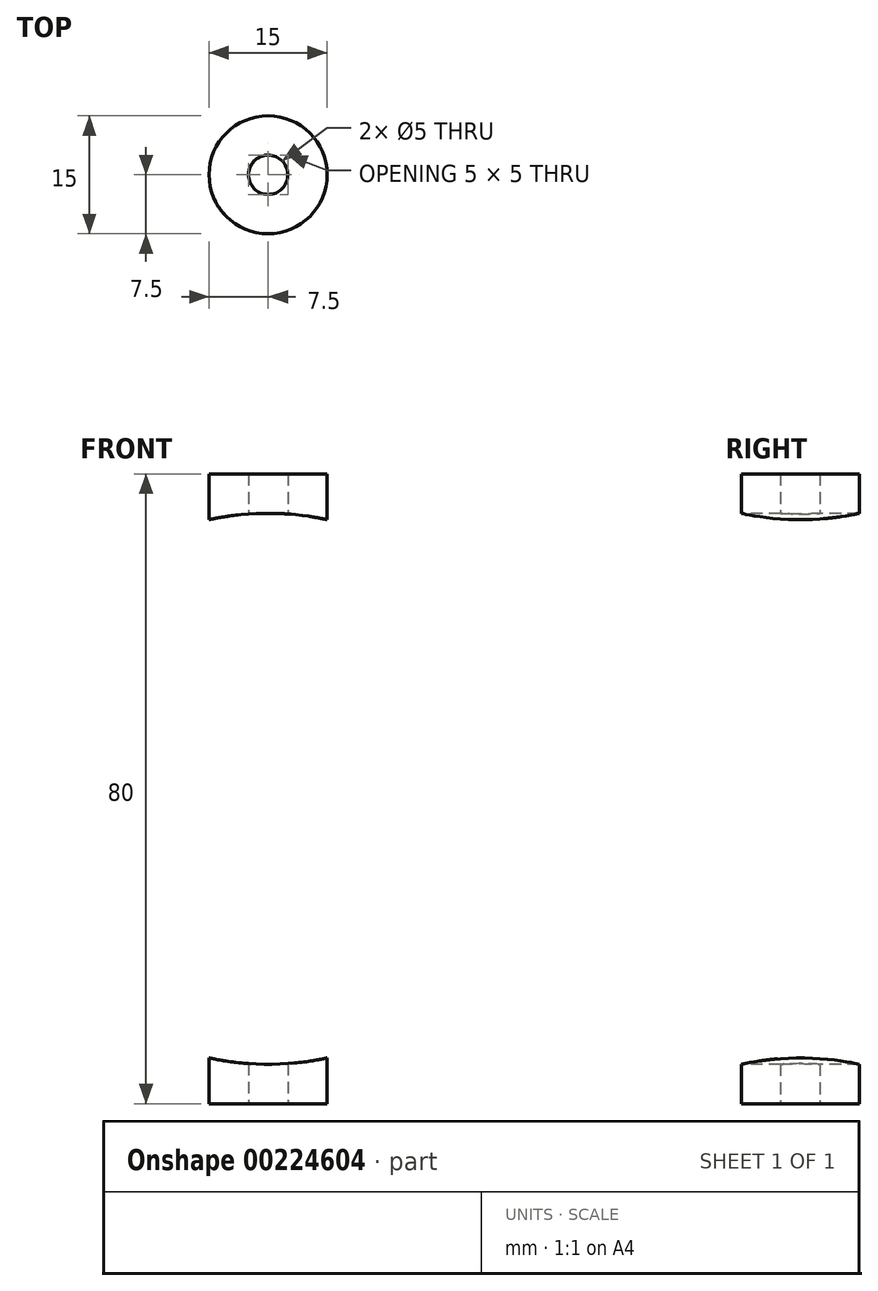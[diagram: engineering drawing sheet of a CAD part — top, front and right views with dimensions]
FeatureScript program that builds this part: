
annotation { "Feature Type Name" : "Feature", "Feature Type Description" : "" }
export const myFeature = defineFeature(function(context is Context, id is Id, definition is map)
    precondition{}
    {
        {
            var Q0;
            Q0=qCreatedBy(makeId("Front.planeOp"),FACE);
            var sketch = newSketch(context, id + "F0", { "sketchPlane" : qUnion([Q0])});
            skCircle(sketch, "E0", {"center": v(0, 40) * mm, "radius": 40 * mm});
            skCircle(sketch, "E1", {"center": v(0, 40) * mm, "radius": 35 * mm});
            skSolve(sketch);
        }
        {
            var Q0;
            Q0=qCreatedBy(makeId("Top.planeOp"),FACE);
            var sketch = newSketch(context, id + "F1", { "sketchPlane" : qUnion([Q0])});
            skCircle(sketch, "E2", {"center": v(0, 0) * mm, "radius": 2.5 * mm});
            skCircle(sketch, "E3", {"center": v(0, 0) * mm, "radius": 7.5 * mm});
            skSolve(sketch);
        }
        {
            var Q0;
            Q0=makeQuery(id+"F0.imprint","IMPRINT",FACE,{"disambiguationData":[TD([[makeQuery(id+"F0.imprint","IMPRINT",EDGE,{"derivedFrom":sQuery(id+"F0.wireOp",EDGE,"E0")}),1.0]])]});
            extrude(context, id + "F2", {"entities" : qUnion([Q0]), "endBound" : BoundingType.SYMMETRIC, "depth" : 5 * mm});
        }
        {
            var Q0;
            Q0=makeQuery(id+"F2.opExtrude","CAP_EDGE",EDGE,{"disambiguationData":[OSD([sQuery(id+"F0.wireOp",EDGE,"E0")])],"isStart":false});
            var Q1;
            Q1=makeQuery(id+"F2.opExtrude","CAP_EDGE",EDGE,{"disambiguationData":[OSD([sQuery(id+"F0.wireOp",EDGE,"E0")])],"isStart":true});
            var Q2;
            Q2=makeQuery(id+"F2.opExtrude","CAP_EDGE",EDGE,{"disambiguationData":[OSD([sQuery(id+"F0.wireOp",EDGE,"E1")])],"isStart":false});
            var Q3;
            Q3=makeQuery(id+"F2.opExtrude","CAP_EDGE",EDGE,{"disambiguationData":[OSD([sQuery(id+"F0.wireOp",EDGE,"E1")])],"isStart":true});
            fillet(context, id + "F3", {"entities" : qUnion([Q0, Q1, Q2, Q3]), "radius" : 2.5 * mm, "tangentPropagation" : true, "allowEdgeOverflow" : false});
        }
        {
            var Q0;
            Q0=makeQuery(id+"F1.imprint","IMPRINT",FACE,{"disambiguationData":[TD([[makeQuery(id+"F1.imprint","IMPRINT",EDGE,{"derivedFrom":sQuery(id+"F1.wireOp",EDGE,"E2")}),-1.0]])]});
            extrude(context, id + "F4", {"entities" : qUnion([Q0]), "operationType" : NewBodyOperationType.REMOVE, "depth" : 80 * mm});
        }
        {
            var Q0;
            Q0=makeQuery(id+"F4.boolean.opBoolean","SPLIT",BODY,{"disambiguationData":[OD(3.0)],"derivedFrom":makeQuery(id+"F2.opExtrude","SWEPT_BODY",BODY,{"disambiguationData":[OSD([sQuery(id+"F0.wireOp",EDGE,"E0"),sQuery(id+"F0.wireOp",EDGE,"E1")])]})});
            var Q1;
            Q1=makeQuery(id+"F4.boolean.opBoolean","SPLIT",BODY,{"disambiguationData":[OD(2.0)],"derivedFrom":makeQuery(id+"F2.opExtrude","SWEPT_BODY",BODY,{"disambiguationData":[OSD([sQuery(id+"F0.wireOp",EDGE,"E0"),sQuery(id+"F0.wireOp",EDGE,"E1")])]})});
            deleteBodies(context, id + "F5", {"entities" : qUnion([Q0, Q1])});
        }
        {
            var Q0;
            Q0=makeQuery(id+"F1.imprint","IMPRINT",FACE,{"disambiguationData":[TD([[makeQuery(id+"F1.imprint","IMPRINT",EDGE,{"derivedFrom":sQuery(id+"F1.wireOp",EDGE,"E2")}),-1.0]])]});
            extrude(context, id + "F6", {"entities" : qUnion([Q0]), "depth" : 80 * mm});
        }
        {
            var Q0;
            Q0=makeQuery(id+"F0.imprint","IMPRINT",FACE,{"disambiguationData":[TD([[makeQuery(id+"F0.imprint","IMPRINT",EDGE,{"derivedFrom":sQuery(id+"F0.wireOp",EDGE,"E1")}),1.0]])]});
            extrude(context, id + "F7", {"entities" : qUnion([Q0]), "operationType" : NewBodyOperationType.REMOVE, "endBound" : BoundingType.SYMMETRIC, "oppositeDirection" : true, "depth" : 80 * mm});
        }
    });
